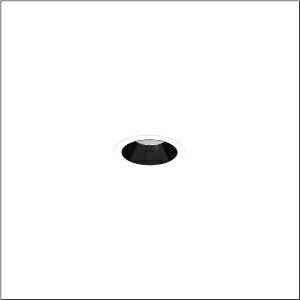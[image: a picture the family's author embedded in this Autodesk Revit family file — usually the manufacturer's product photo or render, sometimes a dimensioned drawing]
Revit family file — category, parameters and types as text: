
# Revit family: lunis_21_s_51db17ma91c
name_source: partatom
category: Lighting Fixtures
units: mm (PartAtom-declared; Revit-internal decimal feet)

## family parameters
Cut with Voids When Loaded = No
Host = Face
Light Source = No
Part Type = Normal
Room Calculation Point = No
Round Connector Dimension = Use Diameter
Shared = No

## types (1)
- --- (1 x LED, 830 lm, 5.9 W, 6500K)
    Apparent Load = 6 VA
    CIE Flux Codes = 97 100 100 100 100
    Color Rendering = 80
    Color Temperature = 6500K
    Default Elevation = 1800 mm
    Description = Lunis 21 S, downlight, light control with lens, of PMMA, anti glare with reflector, of PC, light emission: direct distribution, LED rated luminous flux: 840lm, light colour: 830/840/865, with terminal, 3-pole, mains connection: 220..240V, AC, 50..60Hz, housing, round, of diecast aluminium, traffic white (RAL 9016), diameter: 84mm, clamping range: 1..40mm, protection rating (complete): IP20, protection rating (on room side): IP54, insulation class (complete): insulation class II (safety insulation), certification: CE, impact resistance: IK03, packaging unit: 1 piece
    Height = 0 mm  [stored 0 ft]
    Lamp = 1 x LED
    Lamp Light Flux = 830 lm
    Lamp Power = 5.9 W
    Lamp count = 1
    Length = 84 mm
    Luminous efficacy = 141 lm/W
    Manufacturer = Siteco
    ModVariant = No
    Model = 51DB17MA91C
    Mounting Place = Ceiling
    Mounting Type = Recessed
    Number of Poles = 1
    OnlyDefault = Yes
    Power Factor = 1
    Product Name = Lunis 21 S
    Product group = downlight
    ProductGroupID = 401
    Protection Class = Protection class II
    Protection Degree = IP 20
    RLX_Detail_Level = 1
    RLX_Emergency_Light_Flux = 0 lm
    RLX_Emergency_Type = 0
    RLX_Emergency_Type_DB = No
    RlxData = <blob elided: 8697 chars, md5=7f6e139d>
    Socket = socket
    Standby Power = 0 W
    System Light Flux = 830 lm
    System Power = 6 W
    Type Comments = individual setting: colour temperature 6500K
    Type Image = l_1290844.jpg
    URL = http://relux.com
    VarID = @adj_036089
    Voltage = 0 V
    Weight = 0.00 kg
    Width = 0 mm  [stored 0 ft]

note: [stored X ft] marks values corroborated as IEEE doubles in the binary element streams (Revit-internal decimal feet)

## geometry (parser evidence)
native form markers: Sweep x9
no freeform markers — native parametric forms only
